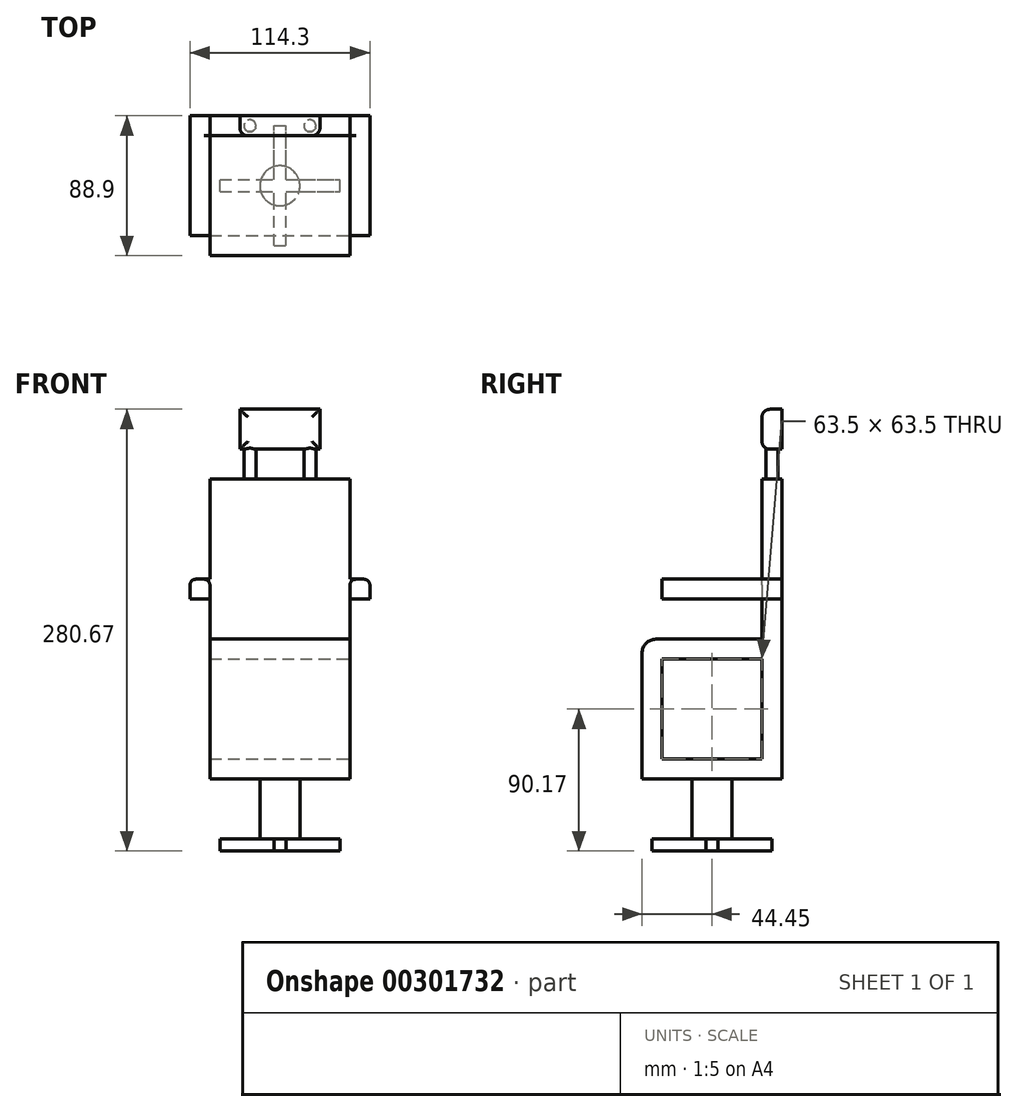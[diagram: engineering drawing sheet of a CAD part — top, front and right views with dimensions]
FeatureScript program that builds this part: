
annotation { "Feature Type Name" : "Feature", "Feature Type Description" : "" }
export const myFeature = defineFeature(function(context is Context, id is Id, definition is map)
    precondition{}
    {
        {
            var Q0;
            Q0=qCreatedBy(makeId("Top.planeOp"),FACE);
            var sketch = newSketch(context, id + "F0", { "sketchPlane" : qUnion([Q0])});
            skLineSegment(sketch, "E0.bottom", {"start": v(44.45, -44.45) * mm, "end": v(-44.45, -44.45) * mm});
            skLineSegment(sketch, "E0.top", {"start": v(44.45, 44.45) * mm, "end": v(-44.45, 44.45) * mm});
            skLineSegment(sketch, "E0.left", {"start": v(44.45, -44.45) * mm, "end": v(44.45, 44.45) * mm});
            skLineSegment(sketch, "E0.right", {"start": v(-44.45, -44.45) * mm, "end": v(-44.45, 44.45) * mm});
            skPoint(sketch, "E0.middle", {"position": v(0, 0) * mm});
            skSolve(sketch);
        }
        {
            var Q0;
            Q0=makeQuery(id+"F0.imprint","IMPRINT",FACE,{"disambiguationData":[TD([[makeQuery(id+"F0.imprint","IMPRINT",EDGE,{"derivedFrom":sQuery(id+"F0.wireOp",EDGE,"E0.bottom")}),-1.0]])]});
            extrude(context, id + "F1", {"entities" : qUnion([Q0]), "depth" : 88.9 * mm});
        }
        {
            var Q0;
            Q0=makeQuery(id+"F1.opExtrude","SWEPT_FACE",FACE,{"disambiguationData":[OSD([sQuery(id+"F0.wireOp",EDGE,"E0.left")])]});
            var sketch = newSketch(context, id + "F2", { "sketchPlane" : qUnion([Q0])});
            skLineSegment(sketch, "E1", {"start": v(0, 96.73) * mm, "end": v(0, -19.94) * mm, "construction": true});
            skLineSegment(sketch, "E2.bottom", {"start": v(31.75, 12.7) * mm, "end": v(-31.75, 12.7) * mm});
            skLineSegment(sketch, "E2.top", {"start": v(31.75, 76.2) * mm, "end": v(-31.75, 76.2) * mm});
            skLineSegment(sketch, "E2.left", {"start": v(31.75, 12.7) * mm, "end": v(31.75, 76.2) * mm});
            skLineSegment(sketch, "E2.right", {"start": v(-31.75, 12.7) * mm, "end": v(-31.75, 76.2) * mm});
            skPoint(sketch, "E2.middle", {"position": v(0, 44.45) * mm});
            skSolve(sketch);
        }
        {
            var Q0;
            Q0=makeQuery(id+"F2.imprint","IMPRINT",FACE,{"disambiguationData":[TD([[makeQuery(id+"F2.imprint","IMPRINT",EDGE,{"derivedFrom":sQuery(id+"F2.wireOp",EDGE,"E2.bottom")}),-1.0]])]});
            extrude(context, id + "F3", {"entities" : qUnion([Q0]), "operationType" : NewBodyOperationType.REMOVE, "oppositeDirection" : true, "depth" : 88.9 * mm});
        }
        {
            var Q0;
            Q0=makeQuery(id+"F1.opExtrude","CAP_FACE",FACE,{"disambiguationData":[OSD([sQuery(id+"F0.wireOp",EDGE,"E0.bottom"),sQuery(id+"F0.wireOp",EDGE,"E0.top"),sQuery(id+"F0.wireOp",EDGE,"E0.left"),sQuery(id+"F0.wireOp",EDGE,"E0.right")])],"isStart":false});
            var sketch = newSketch(context, id + "F4", { "sketchPlane" : qUnion([Q0])});
            skLineSegment(sketch, "E3.bottom", {"start": v(-44.45, 44.45) * mm, "end": v(44.45, 44.45) * mm});
            skLineSegment(sketch, "E3.top", {"start": v(-44.45, 44.45) * mm, "end": v(44.45, 44.45) * mm});
            skLineSegment(sketch, "E3.left", {"start": v(-44.45, 44.45) * mm, "end": v(-44.45, 44.45) * mm});
            skLineSegment(sketch, "E3.right", {"start": v(44.45, 44.45) * mm, "end": v(44.45, 44.45) * mm});
            skLineSegment(sketch, "E4.top", {"start": v(-44.45, 31.75) * mm, "end": v(44.45, 31.75) * mm});
            skLineSegment(sketch, "E4.left", {"start": v(-44.45, 44.45) * mm, "end": v(-44.45, 31.75) * mm});
            skLineSegment(sketch, "E4.right", {"start": v(44.45, 44.45) * mm, "end": v(44.45, 31.75) * mm});
            skSolve(sketch);
        }
        {
            var Q0;
            Q0=makeQuery(id+"F4.imprint","IMPRINT",FACE,{"disambiguationData":[TD([[makeQuery(id+"F4.imprint","IMPRINT",EDGE,{"derivedFrom":sQuery(id+"F4.wireOp",EDGE,"E3.bottom")}),1.0]])]});
            extrude(context, id + "F5", {"entities" : qUnion([Q0]), "operationType" : NewBodyOperationType.ADD, "depth" : 101.6 * mm});
        }
        {
            var Q0;
            Q0=makeQuery(id+"F1.opExtrude","CAP_FACE",FACE,{"disambiguationData":[OSD([sQuery(id+"F0.wireOp",EDGE,"E0.bottom"),sQuery(id+"F0.wireOp",EDGE,"E0.top"),sQuery(id+"F0.wireOp",EDGE,"E0.left"),sQuery(id+"F0.wireOp",EDGE,"E0.right")])],"isStart":true});
            var sketch = newSketch(context, id + "F6", { "sketchPlane" : qUnion([Q0])});
            skCircle(sketch, "E5", {"center": v(0, 0) * mm, "radius": 12.7 * mm});
            skSolve(sketch);
        }
        {
            var Q0;
            Q0=makeQuery(id+"F6.imprint","IMPRINT",FACE,{"disambiguationData":[TD([[makeQuery(id+"F6.imprint","IMPRINT",EDGE,{"derivedFrom":sQuery(id+"F6.wireOp",EDGE,"E5")}),1.0]])]});
            extrude(context, id + "F7", {"entities" : qUnion([Q0]), "operationType" : NewBodyOperationType.ADD, "depth" : 38.1 * mm});
        }
        {
            var Q0;
            Q0=makeQuery(id+"F7.opExtrude","CAP_FACE",FACE,{"disambiguationData":[OSD([sQuery(id+"F6.wireOp",EDGE,"E5")])],"isStart":false});
            var sketch = newSketch(context, id + "F8", { "sketchPlane" : qUnion([Q0])});
            skLineSegment(sketch, "E6.bottom", {"start": v(-3.81, 38.1) * mm, "end": v(3.8, 38.1) * mm});
            skLineSegment(sketch, "E6.top", {"start": v(-3.8, -38.1) * mm, "end": v(3.81, -38.1) * mm});
            skLineSegment(sketch, "E6.left", {"start": v(-3.81, 38.1) * mm, "end": v(-3.8, -38.1) * mm});
            skLineSegment(sketch, "E6.right", {"start": v(3.8, 38.1) * mm, "end": v(3.81, -38.1) * mm});
            skPoint(sketch, "E6.middle", {"position": v(0, 0) * mm});
            skLineSegment(sketch, "E7.bottom", {"start": v(-38.1, 3.8) * mm, "end": v(38.1, 3.8) * mm});
            skLineSegment(sketch, "E7.top", {"start": v(-38.1, -3.81) * mm, "end": v(38.1, -3.81) * mm});
            skLineSegment(sketch, "E7.left", {"start": v(-38.1, 3.8) * mm, "end": v(-38.1, -3.81) * mm});
            skLineSegment(sketch, "E7.right", {"start": v(38.1, 3.8) * mm, "end": v(38.1, -3.81) * mm});
            skSolve(sketch);
        }
        {
            var Q0;
            Q0 = qSketchRegion(id + "F8", true);
            extrude(context, id + "F9", {"entities" : qUnion([Q0]), "operationType" : NewBodyOperationType.ADD, "depth" : 7.62 * mm});
        }
        {
            var Q0;
            Q0=makeQuery(id+"F5.boolean.opBoolean","MERGE",FACE,{"derivedFrom":[makeQuery(id+"F1.opExtrude","SWEPT_FACE",FACE,{"disambiguationData":[OSD([sQuery(id+"F0.wireOp",EDGE,"E0.left")])]}),makeQuery(id+"F5.opExtrude","SWEPT_FACE",FACE,{"disambiguationData":[OSD([sQuery(id+"F4.wireOp",EDGE,"E4.right")])]})]});
            var sketch = newSketch(context, id + "F10", { "sketchPlane" : qUnion([Q0])});
            skLineSegment(sketch, "E8.bottom", {"start": v(44.45, 127) * mm, "end": v(-31.75, 127) * mm});
            skLineSegment(sketch, "E8.top", {"start": v(44.45, 114.3) * mm, "end": v(-31.75, 114.3) * mm});
            skLineSegment(sketch, "E8.left", {"start": v(44.45, 127) * mm, "end": v(44.45, 114.3) * mm});
            skLineSegment(sketch, "E8.right", {"start": v(-31.75, 127) * mm, "end": v(-31.75, 114.3) * mm});
            skSolve(sketch);
        }
        {
            var Q0;
            Q0 = qSketchRegion(id + "F10", true);
            extrude(context, id + "F11", {"entities" : qUnion([Q0]), "operationType" : NewBodyOperationType.ADD, "depth" : 12.7 * mm});
        }
        {
            var Q0;
            Q0=makeQuery(id+"F5.boolean.opBoolean","MERGE",FACE,{"derivedFrom":[makeQuery(id+"F1.opExtrude","SWEPT_FACE",FACE,{"disambiguationData":[OSD([sQuery(id+"F0.wireOp",EDGE,"E0.right")])]}),makeQuery(id+"F5.opExtrude","SWEPT_FACE",FACE,{"disambiguationData":[OSD([sQuery(id+"F4.wireOp",EDGE,"E4.left")])]})]});
            var sketch = newSketch(context, id + "F12", { "sketchPlane" : qUnion([Q0])});
            skLineSegment(sketch, "E9.bottom", {"start": v(-44.45, 114.3) * mm, "end": v(31.75, 114.3) * mm});
            skLineSegment(sketch, "E9.top", {"start": v(-44.45, 127) * mm, "end": v(31.75, 127) * mm});
            skLineSegment(sketch, "E9.left", {"start": v(-44.45, 114.3) * mm, "end": v(-44.45, 127) * mm});
            skLineSegment(sketch, "E9.right", {"start": v(31.75, 114.3) * mm, "end": v(31.75, 127) * mm});
            skSolve(sketch);
        }
        {
            var Q0;
            Q0 = qSketchRegion(id + "F12", true);
            extrude(context, id + "F13", {"entities" : qUnion([Q0]), "operationType" : NewBodyOperationType.ADD, "depth" : 12.7 * mm});
        }
        {
            var Q0;
            Q0=makeQuery(id+"F5.opExtrude","CAP_FACE",FACE,{"disambiguationData":[OSD([sQuery(id+"F4.wireOp",EDGE,"E3.bottom"),sQuery(id+"F4.wireOp",EDGE,"E4.top"),sQuery(id+"F4.wireOp",EDGE,"E4.left"),sQuery(id+"F4.wireOp",EDGE,"E4.right")])],"isStart":false});
            var sketch = newSketch(context, id + "F14", { "sketchPlane" : qUnion([Q0])});
            skCircle(sketch, "E10", {"center": v(-19.05, 38.1) * mm, "radius": 3.81 * mm});
            skCircle(sketch, "E11", {"center": v(19.05, 38.1) * mm, "radius": 3.81 * mm});
            skSolve(sketch);
        }
        {
            var Q0;
            Q0=makeQuery(id+"F14.imprint","IMPRINT",FACE,{"disambiguationData":[TD([[makeQuery(id+"F14.imprint","IMPRINT",EDGE,{"derivedFrom":sQuery(id+"F14.wireOp",EDGE,"E11")}),1.0]])]});
            var Q1;
            Q1=makeQuery(id+"F14.imprint","IMPRINT",FACE,{"disambiguationData":[TD([[makeQuery(id+"F14.imprint","IMPRINT",EDGE,{"derivedFrom":sQuery(id+"F14.wireOp",EDGE,"E10")}),1.0]])]});
            extrude(context, id + "F15", {"entities" : qUnion([Q0, Q1]), "operationType" : NewBodyOperationType.ADD, "depth" : 19.05 * mm});
        }
        {
            var Q0;
            Q0=makeQuery(id+"F15.opExtrude","CAP_FACE",FACE,{"disambiguationData":[OSD([sQuery(id+"F14.wireOp",EDGE,"E10")])],"isStart":false});
            var sketch = newSketch(context, id + "F16", { "sketchPlane" : qUnion([Q0])});
            skLineSegment(sketch, "E12.bottom", {"start": v(25.4, 31.75) * mm, "end": v(-25.4, 31.75) * mm});
            skLineSegment(sketch, "E12.top", {"start": v(25.4, 44.45) * mm, "end": v(-25.4, 44.45) * mm});
            skLineSegment(sketch, "E12.left", {"start": v(25.4, 31.75) * mm, "end": v(25.4, 44.45) * mm});
            skLineSegment(sketch, "E12.right", {"start": v(-25.4, 31.75) * mm, "end": v(-25.4, 44.45) * mm});
            skPoint(sketch, "E12.middle", {"position": v(0, 38.1) * mm});
            skSolve(sketch);
        }
        {
            var Q0;
            Q0 = qSketchRegion(id + "F16", true);
            extrude(context, id + "F17", {"entities" : qUnion([Q0]), "operationType" : NewBodyOperationType.ADD, "depth" : 25.4 * mm});
        }
        {
            var Q0;
            Q0=makeQuery(id+"F1.opExtrude","CAP_EDGE",EDGE,{"disambiguationData":[OSD([sQuery(id+"F0.wireOp",EDGE,"E0.bottom")])],"isStart":false});
            fillet(context, id + "F18", {"entities" : qUnion([Q0]), "radius" : 8.9 * mm, "tangentPropagation" : true, "allowEdgeOverflow" : false});
        }
        {
            var Q0;
            Q0=makeQuery(id+"F17.opExtrude","CAP_EDGE",EDGE,{"disambiguationData":[OSD([sQuery(id+"F16.wireOp",EDGE,"E12.bottom")])],"isStart":false});
            var Q1;
            Q1=makeQuery(id+"F17.opExtrude","CAP_EDGE",EDGE,{"disambiguationData":[OSD([sQuery(id+"F16.wireOp",EDGE,"E12.bottom")])],"isStart":true});
            var Q2;
            Q2=makeQuery(id+"F17.opExtrude","SWEPT_EDGE",EDGE,{"disambiguationData":[OSD([sQuery(id+"F16.wireOp",EDGE,"E12.bottom"),sQuery(id+"F16.wireOp",EDGE,"E12.left")])]});
            var Q3;
            Q3=makeQuery(id+"F17.opExtrude","SWEPT_EDGE",EDGE,{"disambiguationData":[OSD([sQuery(id+"F16.wireOp",EDGE,"E12.bottom"),sQuery(id+"F16.wireOp",EDGE,"E12.right")])]});
            fillet(context, id + "F19", {"entities" : qUnion([Q0, Q1, Q2, Q3]), "radius" : 5.08 * mm, "tangentPropagation" : true, "allowEdgeOverflow" : false});
        }
        {
            var Q0;
            {var subQ0=sQuery(id+"F10.wireOp",EDGE,"E8.bottom");Q0=makeQuery(id+"F11.boolean.opBoolean","SPLIT",EDGE,{"disambiguationData":[topologyDisambiguationEdgeConnected([makeQuery(id+"F11.opExtrude","CAP_FACE",FACE,{"disambiguationData":[OSD([subQ0,sQuery(id+"F10.wireOp",EDGE,"E8.top"),sQuery(id+"F10.wireOp",EDGE,"E8.left"),sQuery(id+"F10.wireOp",EDGE,"E8.right")])],"isStart":true})])],"derivedFrom":makeQuery(id+"F11.opExtrude","CAP_EDGE",EDGE,{"disambiguationData":[OSD([subQ0])],"isStart":true})});}
            var Q1;
            Q1=makeQuery(id+"F11.opExtrude","CAP_EDGE",EDGE,{"disambiguationData":[OSD([sQuery(id+"F10.wireOp",EDGE,"E8.bottom")])],"isStart":false});
            var Q2;
            {var subQ0=sQuery(id+"F12.wireOp",EDGE,"E9.top");Q2=makeQuery(id+"F13.boolean.opBoolean","SPLIT",EDGE,{"disambiguationData":[topologyDisambiguationEdgeConnected([makeQuery(id+"F13.opExtrude","CAP_FACE",FACE,{"disambiguationData":[OSD([sQuery(id+"F12.wireOp",EDGE,"E9.bottom"),subQ0,sQuery(id+"F12.wireOp",EDGE,"E9.left"),sQuery(id+"F12.wireOp",EDGE,"E9.right")])],"isStart":true})])],"derivedFrom":makeQuery(id+"F13.opExtrude","CAP_EDGE",EDGE,{"disambiguationData":[OSD([subQ0])],"isStart":true})});}
            var Q3;
            Q3=makeQuery(id+"F13.opExtrude","CAP_EDGE",EDGE,{"disambiguationData":[OSD([sQuery(id+"F12.wireOp",EDGE,"E9.top")])],"isStart":false});
            fillet(context, id + "F20", {"entities" : qUnion([Q0, Q1, Q2, Q3]), "radius" : 3.8 * mm, "tangentPropagation" : true, "allowEdgeOverflow" : false});
        }
    });
